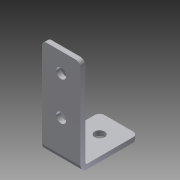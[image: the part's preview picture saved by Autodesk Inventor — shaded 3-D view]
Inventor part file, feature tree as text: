
AUTODESK INVENTOR PART (.ipt)
format: ipt  version: 2013 (Build 170138000, 138)  size: 182,784 bytes
history: native  units: in
note: dims shown in document units (in); Inventor stores cm internally (conversion verified against a paired STEP export)
features: sheet_metal_op x4, other x4, sketch x3, chamfer x1
ambient origin geometry x8: Origin, YZ Plane, XZ Plane, XY Plane, X Axis, Y Axis, Z Axis, Center Point
bodies: Solid1 (feature_tree)
feature tree (12):
  sheet_metal_op  "Face1"
  sheet_metal_op  "Flange1"
  chamfer  "Corner Round1"
  sketch  "Sketch1"  dims[d0=0.26in]
  other  "Plate1"
  sketch  "Sketch2"  dims[d2=1.0in]
  other  "Plate2"
  sheet_metal_op  "Bend1"
  sheet_metal_op  "Corner1"
  sketch  "Sketch3"  dims[d3=1.5in d4=0.625in d5=0.375in d6=0.125in d7=0.125in d8=0.0625in d9=0.25in d10=0.125in d11=2.5in d12=90.0deg d13=0.05in d14=0.5in d15=0.125in d16=0.125in d17=1.0in d18=1.0in d19=0.26in d20=0.125in d21=0.0in d22=0.125in]
  other  "Cut1"
  other  "Definition1"
